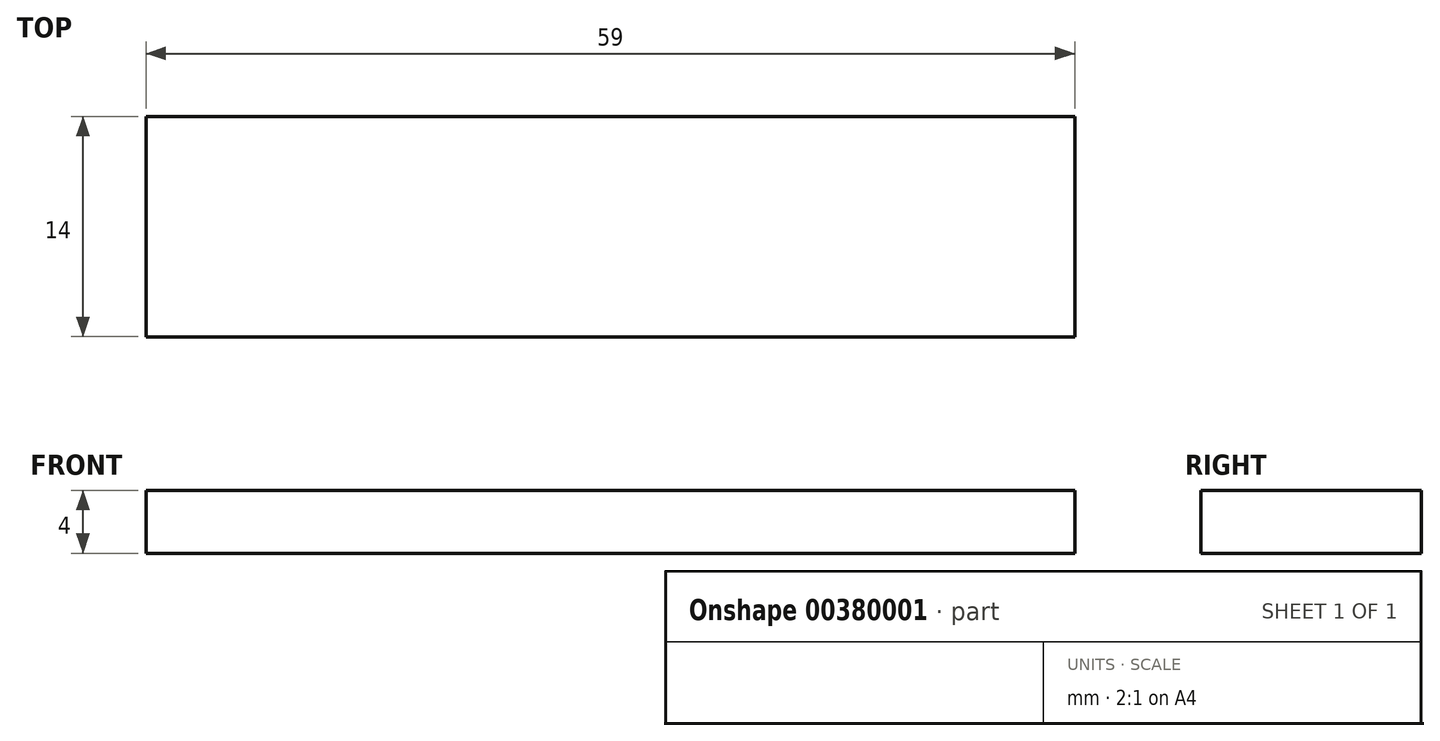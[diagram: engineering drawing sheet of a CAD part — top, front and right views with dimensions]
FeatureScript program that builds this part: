
annotation { "Feature Type Name" : "Feature", "Feature Type Description" : "" }
export const myFeature = defineFeature(function(context is Context, id is Id, definition is map)
    precondition{}
    {
        {
            var Q0;
            Q0=qCreatedBy(makeId("Top.planeOp"),FACE);
            var sketch = newSketch(context, id + "F0", { "sketchPlane" : qUnion([Q0])});
            skLineSegment(sketch, "E0.bottom", {"start": v(-10.22, -14.72) * mm, "end": v(48.78, -14.72) * mm});
            skLineSegment(sketch, "E0.top", {"start": v(-10.22, -28.72) * mm, "end": v(48.78, -28.72) * mm});
            skLineSegment(sketch, "E0.left", {"start": v(-10.22, -14.72) * mm, "end": v(-10.22, -28.72) * mm});
            skLineSegment(sketch, "E0.right", {"start": v(48.78, -14.72) * mm, "end": v(48.78, -28.72) * mm});
            skSolve(sketch);
        }
        {
            var Q0;
            Q0=makeQuery(id+"F0.imprint","IMPRINT",FACE,{"disambiguationData":[TD([[makeQuery(id+"F0.imprint","IMPRINT",EDGE,{"derivedFrom":sQuery(id+"F0.wireOp",EDGE,"E0.bottom")}),-1.0]])]});
            extrude(context, id + "F1", {"entities" : qUnion([Q0]), "depth" : 4 * mm});
        }
    });
